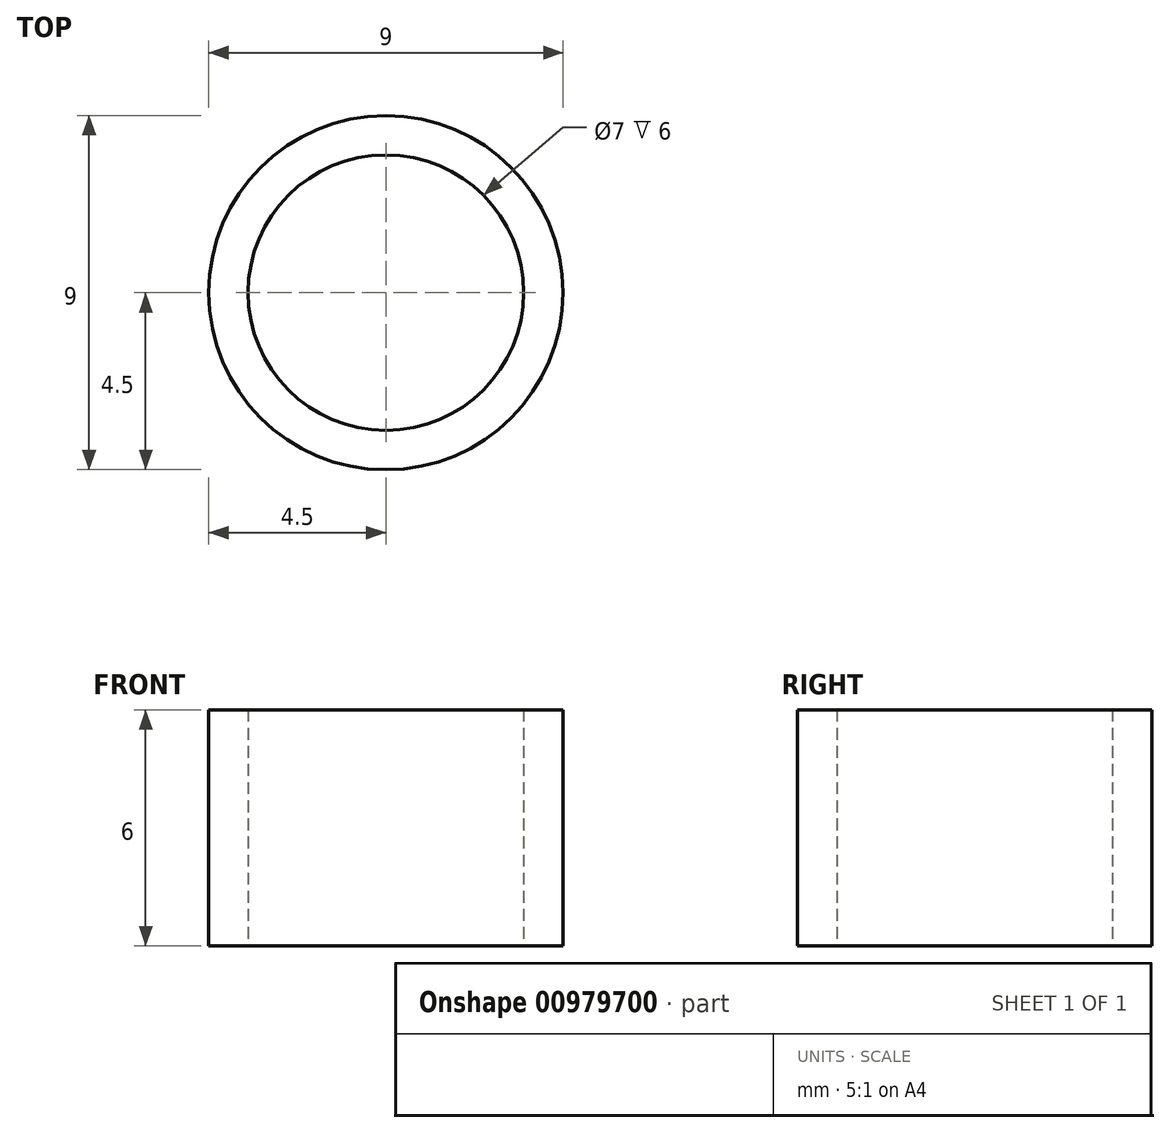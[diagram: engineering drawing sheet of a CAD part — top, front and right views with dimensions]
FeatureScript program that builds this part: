
annotation { "Feature Type Name" : "Feature", "Feature Type Description" : "" }
export const myFeature = defineFeature(function(context is Context, id is Id, definition is map)
    precondition{}
    {
        {
            var Q0;
            Q0=qCreatedBy(makeId("Top.planeOp"),FACE);
            var sketch = newSketch(context, id + "F0", { "sketchPlane" : qUnion([Q0])});
            skCircle(sketch, "E0", {"center": v(0, 0) * mm, "radius": 3.5 * mm});
            skCircle(sketch, "E1", {"center": v(0, 0) * mm, "radius": 4.5 * mm});
            skSolve(sketch);
        }
        {
            var Q0;
            Q0 = qSketchRegion(id + "F0", true);
            extrude(context, id + "F1", {"entities" : qUnion([Q0]), "depth" : 6 * mm, "offsetDistance" : 25 * mm});
        }
    });
